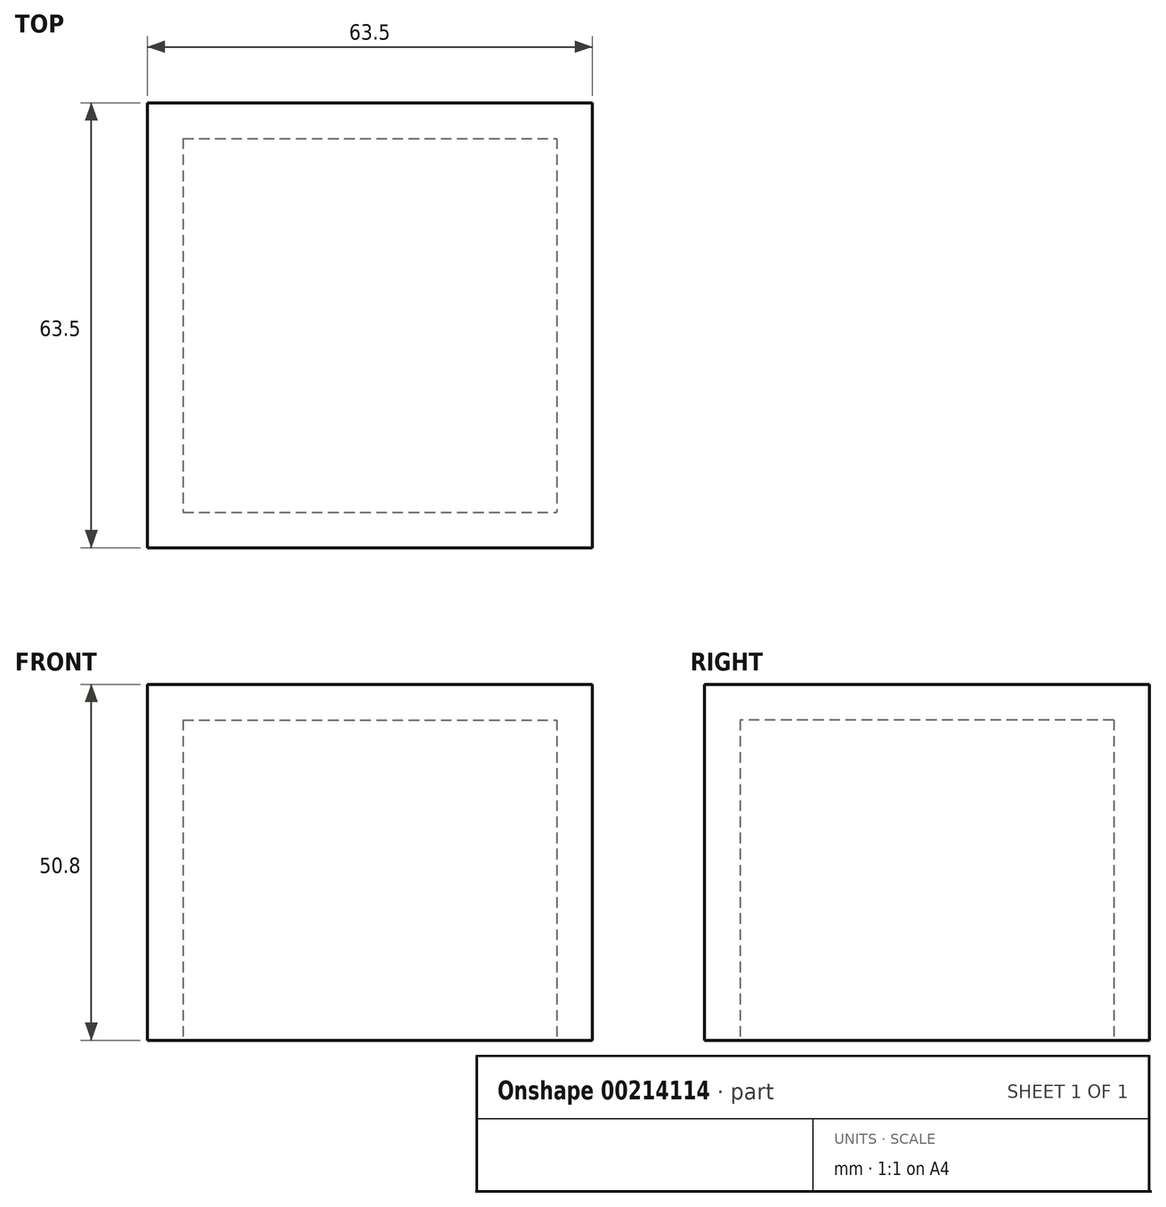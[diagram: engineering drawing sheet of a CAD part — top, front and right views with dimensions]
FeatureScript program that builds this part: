
annotation { "Feature Type Name" : "Feature", "Feature Type Description" : "" }
export const myFeature = defineFeature(function(context is Context, id is Id, definition is map)
    precondition{}
    {
        {
            var Q0;
            Q0=qCreatedBy(makeId("Top.planeOp"),FACE);
            var sketch = newSketch(context, id + "F0", { "sketchPlane" : qUnion([Q0])});
            skLineSegment(sketch, "E0.bottom", {"start": v(-31.75, 31.75) * mm, "end": v(31.75, 31.75) * mm});
            skLineSegment(sketch, "E0.top", {"start": v(-31.75, -31.75) * mm, "end": v(31.75, -31.75) * mm});
            skLineSegment(sketch, "E0.left", {"start": v(-31.75, 31.75) * mm, "end": v(-31.75, -31.75) * mm});
            skLineSegment(sketch, "E0.right", {"start": v(31.75, 31.75) * mm, "end": v(31.75, -31.75) * mm});
            skPoint(sketch, "E0.middle", {"position": v(0, 0) * mm});
            skSolve(sketch);
        }
        {
            var Q0;
            Q0=makeQuery(id+"F0.imprint","IMPRINT",FACE,{"disambiguationData":[TD([[makeQuery(id+"F0.imprint","IMPRINT",EDGE,{"derivedFrom":sQuery(id+"F0.wireOp",EDGE,"E0.bottom")}),-1.0]])]});
            extrude(context, id + "F1", {"entities" : qUnion([Q0]), "depth" : 50.8 * mm});
        }
        {
            var Q0;
            Q0=makeQuery(id+"F1.opExtrude","CAP_FACE",FACE,{"disambiguationData":[OSD([sQuery(id+"F0.wireOp",EDGE,"E0.bottom"),sQuery(id+"F0.wireOp",EDGE,"E0.top"),sQuery(id+"F0.wireOp",EDGE,"E0.left"),sQuery(id+"F0.wireOp",EDGE,"E0.right")])],"isStart":true});
            shell(context, id + "F2", {"entities" : qUnion([Q0]), "thickness" : 5.08 * mm});
        }
    });
